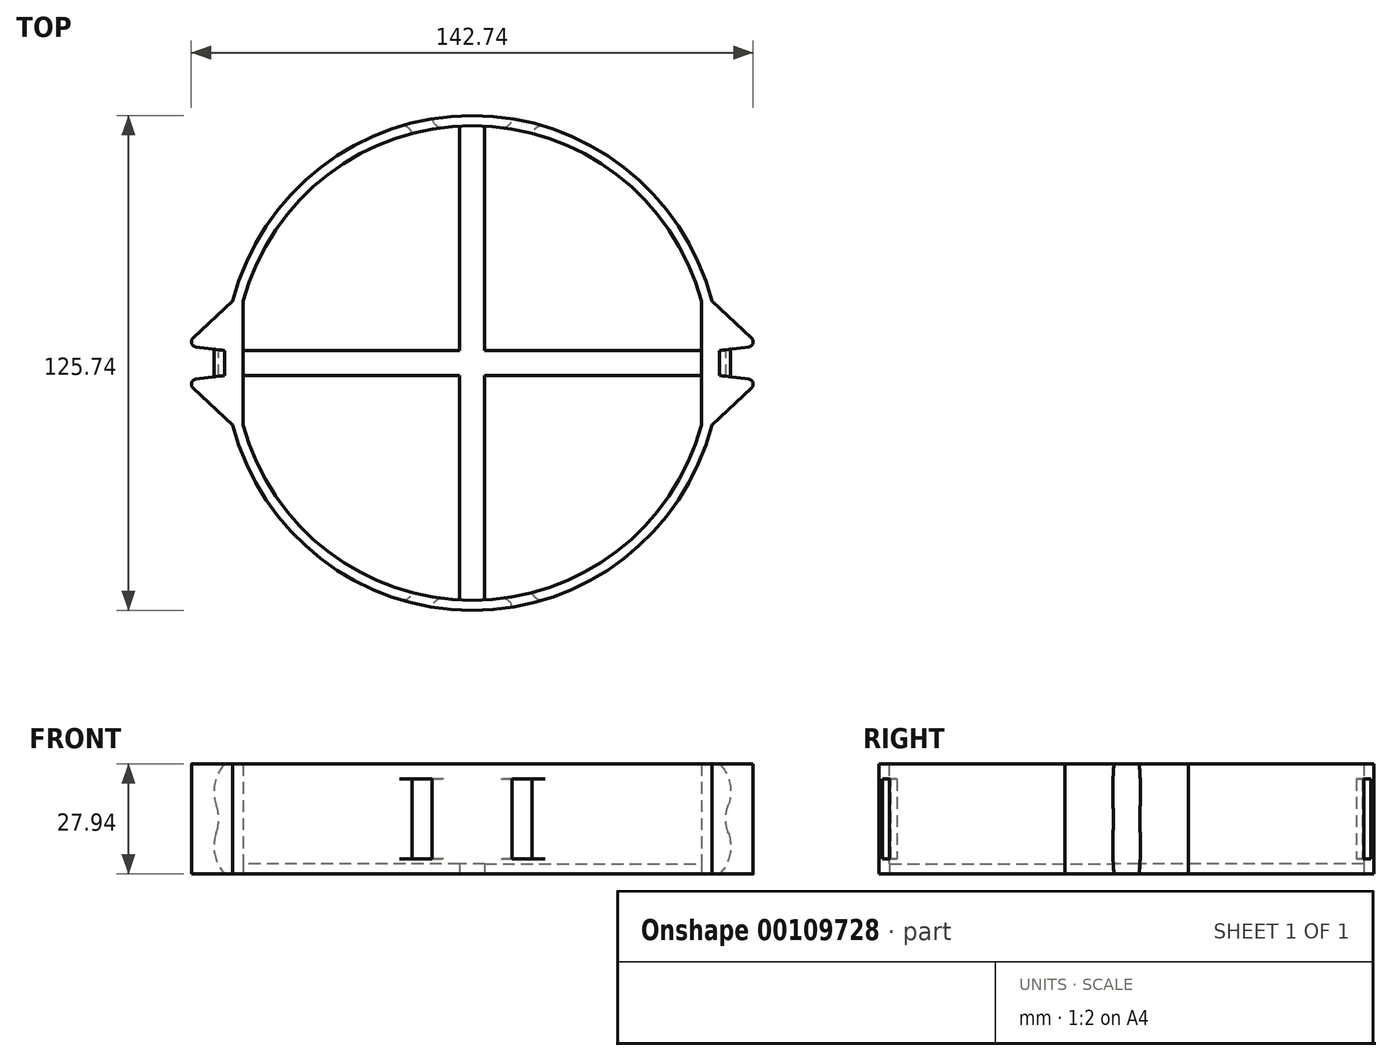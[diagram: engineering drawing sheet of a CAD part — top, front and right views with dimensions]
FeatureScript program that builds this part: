
annotation { "Feature Type Name" : "Feature", "Feature Type Description" : "" }
export const myFeature = defineFeature(function(context is Context, id is Id, definition is map)
    precondition{}
    {
        {
            var Q0;
            Q0=qCreatedBy(makeId("Top.planeOp"),FACE);
            var sketch = newSketch(context, id + "F0", { "sketchPlane" : qUnion([Q0])});
            skCircle(sketch, "E0", {"center": v(0, 0) * mm, "radius": 60.33 * mm});
            skCircle(sketch, "E1", {"center": v(0, 0) * mm, "radius": 62.87 * mm});
            skLineSegment(sketch, "E2", {"start": v(109.73, 0) * mm, "end": v(0, 0) * mm, "construction": true});
            skLineSegment(sketch, "E3", {"start": v(62.87, -3.18) * mm, "end": v(62.87, 3.17) * mm});
            skLineSegment(sketch, "E4", {"start": v(62.87, 3.17) * mm, "end": v(70.25, 4.1) * mm});
            skLineSegment(sketch, "E5", {"start": v(62.87, -3.18) * mm, "end": v(70.25, -4.1) * mm});
            skLineSegment(sketch, "E6", {"start": v(70.96, 6.3) * mm, "end": v(60.87, 15.7) * mm});
            skLineSegment(sketch, "E7", {"start": v(70.96, -6.3) * mm, "end": v(60.87, -15.7) * mm});
            skPoint(sketch, "E8.visualSharp", {"position": v(72.95, 4.44) * mm});
            skArc(sketch, "E8.filletArc", {"start": v(70.25, 4.1) * mm, "mid": v(71.3, 4.98) * mm, "end": v(70.96, 6.3) * mm});
            skPoint(sketch, "E9.visualSharp", {"position": v(72.95, -4.45) * mm});
            skArc(sketch, "E9.filletArc", {"start": v(70.96, -6.3) * mm, "mid": v(71.3, -4.98) * mm, "end": v(70.25, -4.1) * mm});
            skLineSegment(sketch, "E10", {"start": v(0, -72.25) * mm, "end": v(0, 0) * mm, "construction": true});
            skLineSegment(sketch, "E11.MirrorCS", {"start": v(-70.96, 6.3) * mm, "end": v(-60.87, 15.7) * mm});
            skArc(sketch, "E12.MirrorCS", {"start": v(-70.25, 4.1) * mm, "mid": v(-71.3, 4.98) * mm, "end": v(-70.96, 6.3) * mm});
            skLineSegment(sketch, "E13.MirrorCS", {"start": v(-62.87, -3.18) * mm, "end": v(-70.25, -4.1) * mm});
            skArc(sketch, "E14.MirrorCS", {"start": v(-70.96, -6.3) * mm, "mid": v(-71.3, -4.98) * mm, "end": v(-70.25, -4.1) * mm});
            skLineSegment(sketch, "E15.MirrorCS", {"start": v(-70.96, -6.3) * mm, "end": v(-60.87, -15.7) * mm});
            skLineSegment(sketch, "E16.MirrorCS", {"start": v(-62.87, 3.17) * mm, "end": v(-70.25, 4.1) * mm});
            skLineSegment(sketch, "E17", {"start": v(-62.87, -3.18) * mm, "end": v(-62.87, 3.17) * mm});
            skLineSegment(sketch, "E18", {"start": v(-60.87, 15.7) * mm, "end": v(-58.24, 15.7) * mm});
            skLineSegment(sketch, "E19", {"start": v(-60.87, -15.7) * mm, "end": v(-58.24, -15.7) * mm});
            skLineSegment(sketch, "E20", {"start": v(-58.24, -15.7) * mm, "end": v(-58.24, 15.7) * mm});
            skLineSegment(sketch, "E21", {"start": v(60.87, 15.7) * mm, "end": v(58.24, 15.7) * mm});
            skLineSegment(sketch, "E22", {"start": v(60.87, -15.7) * mm, "end": v(58.24, -15.7) * mm});
            skLineSegment(sketch, "E23", {"start": v(58.24, -15.7) * mm, "end": v(58.24, 15.7) * mm});
            skSolve(sketch);
        }
        {
            var Q0;
            {var subQ0=sQuery(id+"F0.wireOp",EDGE,"E15.MirrorCS");Q0=makeQuery(id+"F0.imprint","IMPRINT",FACE,{"disambiguationData":[TD([[makeQuery(id+"F0.imprint","IMPRINT",EDGE,{"derivedFrom":subQ0}),1.0]])]});}
            var Q1;
            Q1=makeQuery(id+"F0.imprint","IMPRINT",FACE,{"disambiguationData":[TD([[makeQuery(id+"F0.imprint","IMPRINT",EDGE,{"derivedFrom":sQuery(id+"F0.wireOp",EDGE,"E0")}),-1.0]])]});
            var Q2;
            {var subQ1=sQuery(id+"F0.wireOp",EDGE,"E4");Q2=makeQuery(id+"F0.imprint","IMPRINT",FACE,{"disambiguationData":[TD([[makeQuery(id+"F0.imprint","IMPRINT",EDGE,{"derivedFrom":subQ1}),1.0]])]});}
            var Q3;
            {var subQ1=sQuery(id+"F0.wireOp",EDGE,"E5");Q3=makeQuery(id+"F0.imprint","IMPRINT",FACE,{"disambiguationData":[TD([[makeQuery(id+"F0.imprint","IMPRINT",EDGE,{"derivedFrom":subQ1}),-1.0]])]});}
            var Q4;
            {var subQ0=sQuery(id+"F0.wireOp",EDGE,"E11.MirrorCS");Q4=makeQuery(id+"F0.imprint","IMPRINT",FACE,{"disambiguationData":[TD([[makeQuery(id+"F0.imprint","IMPRINT",EDGE,{"derivedFrom":subQ0}),-1.0]])]});}
            var Q5;
            {var subQ0=sQuery(id+"F0.wireOp",EDGE,"E23");Q5=makeQuery(id+"F0.imprint","IMPRINT",FACE,{"disambiguationData":[TD([[makeQuery(id+"F0.imprint","IMPRINT",EDGE,{"derivedFrom":subQ0}),-1.0]])]});}
            var Q6;
            {var subQ0=sQuery(id+"F0.wireOp",EDGE,"E21");Q6=makeQuery(id+"F0.imprint","IMPRINT",FACE,{"disambiguationData":[TD([[makeQuery(id+"F0.imprint","IMPRINT",EDGE,{"derivedFrom":subQ0}),1.0]])]});}
            var Q7;
            {var subQ0=sQuery(id+"F0.wireOp",EDGE,"E18");Q7=makeQuery(id+"F0.imprint","IMPRINT",FACE,{"disambiguationData":[TD([[makeQuery(id+"F0.imprint","IMPRINT",EDGE,{"derivedFrom":subQ0}),-1.0]])]});}
            var Q8;
            {var subQ0=sQuery(id+"F0.wireOp",EDGE,"E20");Q8=makeQuery(id+"F0.imprint","IMPRINT",FACE,{"disambiguationData":[TD([[makeQuery(id+"F0.imprint","IMPRINT",EDGE,{"derivedFrom":subQ0}),1.0]])]});}
            extrude(context, id + "F1", {"entities" : qUnion([Q0, Q1, Q2, Q3, Q4, Q5, Q6, Q7, Q8]), "depth" : 27.94 * mm});
        }
        {
            var Q0;
            Q0=makeQuery(id+"F1.opExtrude","CAP_FACE",FACE,{"disambiguationData":[OSD([sQuery(id+"F0.wireOp",EDGE,"E0"),sQuery(id+"F0.wireOp",EDGE,"E1"),sQuery(id+"F0.wireOp",EDGE,"E3"),sQuery(id+"F0.wireOp",EDGE,"E4"),sQuery(id+"F0.wireOp",EDGE,"E5"),sQuery(id+"F0.wireOp",EDGE,"E6"),sQuery(id+"F0.wireOp",EDGE,"E7"),sQuery(id+"F0.wireOp",EDGE,"E8.filletArc"),sQuery(id+"F0.wireOp",EDGE,"E9.filletArc"),sQuery(id+"F0.wireOp",EDGE,"E11.MirrorCS"),sQuery(id+"F0.wireOp",EDGE,"E15.MirrorCS"),sQuery(id+"F0.wireOp",EDGE,"E12.MirrorCS"),sQuery(id+"F0.wireOp",EDGE,"E16.MirrorCS"),sQuery(id+"F0.wireOp",EDGE,"E14.MirrorCS"),sQuery(id+"F0.wireOp",EDGE,"E13.MirrorCS"),sQuery(id+"F0.wireOp",EDGE,"E17"),sQuery(id+"F0.wireOp",EDGE,"E20"),sQuery(id+"F0.wireOp",EDGE,"E23")])],"isStart":true});
            var sketch = newSketch(context, id + "F2", { "sketchPlane" : qUnion([Q0])});
            skLineSegment(sketch, "E24.0", {"start": v(62.87, 3.18) * mm, "end": v(62.87, -3.17) * mm});
            skLineSegment(sketch, "E25.0", {"start": v(-62.87, 3.18) * mm, "end": v(-62.87, -3.17) * mm});
            skLineSegment(sketch, "E26", {"start": v(-62.87, 3.18) * mm, "end": v(62.87, 3.18) * mm});
            skLineSegment(sketch, "E27", {"start": v(62.87, -3.17) * mm, "end": v(-62.87, -3.18) * mm});
            skLineSegment(sketch, "E28", {"start": v(0, 0) * mm, "end": v(0, 111.99) * mm, "construction": true});
            skLineSegment(sketch, "E29", {"start": v(3.18, 3.18) * mm, "end": v(3.18, 60.24) * mm});
            skLineSegment(sketch, "E30", {"start": v(-3.18, 60.24) * mm, "end": v(-3.17, 3.18) * mm});
            skLineSegment(sketch, "E31", {"start": v(-3.17, 3.18) * mm, "end": v(-3.17, -60.24) * mm});
            skLineSegment(sketch, "E32", {"start": v(3.18, -60.24) * mm, "end": v(3.18, 3.18) * mm});
            skSolve(sketch);
        }
        {
            var Q0;
            Q0 = qSketchRegion(id + "F2", true);
            var Q1;
            {var subQ0=sQuery(id+"F2.wireOp",EDGE,"E29");Q1=makeQuery(id+"F2.imprint","IMPRINT",FACE,{"disambiguationData":[TD([[makeQuery(id+"F2.imprint","IMPRINT",EDGE,{"derivedFrom":subQ0}),1.0]])]});}
            var Q2;
            {var subQ0=sQuery(id+"F2.wireOp",EDGE,"E32");var subQ1=sQuery(id+"F2.wireOp",EDGE,"E27");var subQ2=makeQuery(id+"F2.imprint","INTERSECT",VERTEX,{"derivedFrom":[subQ1,subQ0]});Q2=makeQuery(id+"F2.imprint","IMPRINT",FACE,{"disambiguationData":[TD([[makeQuery(id+"F2.imprint","IMPRINT",EDGE,{"disambiguationData":[TD([[subQ2,-1.0]])],"derivedFrom":subQ1}),1.0]])]});}
            extrude(context, id + "F3", {"entities" : qUnion([Q0, Q1, Q2]), "operationType" : NewBodyOperationType.ADD, "oppositeDirection" : true, "depth" : 2.54 * mm});
        }
        {
            var Q0;
            Q0=qCreatedBy(makeId("Front.planeOp"),FACE);
            var sketch = newSketch(context, id + "F4", { "sketchPlane" : qUnion([Q0])});
            skLineSegment(sketch, "E33.bottom", {"start": v(-10.16, 24.13) * mm, "end": v(-15.24, 24.13) * mm});
            skLineSegment(sketch, "E33.top", {"start": v(-10.16, 3.8) * mm, "end": v(-15.24, 3.8) * mm});
            skLineSegment(sketch, "E33.left", {"start": v(-10.16, 24.13) * mm, "end": v(-10.16, 3.8) * mm});
            skLineSegment(sketch, "E33.right", {"start": v(-15.24, 24.13) * mm, "end": v(-15.24, 3.8) * mm});
            skLineSegment(sketch, "E34.bottom", {"start": v(10.16, 24.13) * mm, "end": v(15.24, 24.13) * mm});
            skLineSegment(sketch, "E34.top", {"start": v(10.16, 3.81) * mm, "end": v(15.24, 3.81) * mm});
            skLineSegment(sketch, "E34.left", {"start": v(10.16, 24.13) * mm, "end": v(10.16, 3.81) * mm});
            skLineSegment(sketch, "E34.right", {"start": v(15.24, 24.13) * mm, "end": v(15.24, 3.81) * mm});
            skSolve(sketch);
        }
        {
            var Q0;
            Q0 = qSketchRegion(id + "F4", true);
            extrude(context, id + "F5", {"entities" : qUnion([Q0]), "operationType" : NewBodyOperationType.REMOVE, "endBound" : BoundingType.THROUGH_ALL, "oppositeDirection" : true, "depth" : 25.4 * mm, "hasSecondDirection" : true, "secondDirectionBound" : SecondDirectionBoundingType.THROUGH_ALL, "secondDirectionOppositeDirection" : false, "secondDirectionDepth" : 25.4 * mm});
        }
        {
            var Q0;
            {var subQ0=sQuery(id+"F0.wireOp",EDGE,"E1");Q0=makeQuery(id+"F5.boolean.opBoolean","INTERSECT",EDGE,{"derivedFrom":[makeQuery(id+"F1.opExtrude","SWEPT_FACE",FACE,{"disambiguationData":[OSD([subQ0]),TDD([makeQuery(id+"F0.imprint","IMPRINT",EDGE,{"disambiguationData":[TD([[makeQuery(id+"F0.imprint","INTERSECT",VERTEX,{"derivedFrom":[subQ0,sQuery(id+"F0.wireOp",EDGE,"E6"),sQuery(id+"F0.wireOp",EDGE,"E21")]}),-1.0]])],"derivedFrom":subQ0})])]}),makeQuery(id+"F5.opExtrude","SWEPT_FACE",FACE,{"disambiguationData":[OSD([sQuery(id+"F4.wireOp",EDGE,"E34.right")])]})]});}
            var Q1;
            {var subQ0=sQuery(id+"F0.wireOp",EDGE,"E1");Q1=makeQuery(id+"F5.boolean.opBoolean","INTERSECT",EDGE,{"derivedFrom":[makeQuery(id+"F1.opExtrude","SWEPT_FACE",FACE,{"disambiguationData":[OSD([subQ0]),TDD([makeQuery(id+"F0.imprint","IMPRINT",EDGE,{"disambiguationData":[TD([[makeQuery(id+"F0.imprint","INTERSECT",VERTEX,{"derivedFrom":[subQ0,sQuery(id+"F0.wireOp",EDGE,"E6"),sQuery(id+"F0.wireOp",EDGE,"E21")]}),-1.0]])],"derivedFrom":subQ0})])]}),makeQuery(id+"F5.opExtrude","SWEPT_FACE",FACE,{"disambiguationData":[OSD([sQuery(id+"F4.wireOp",EDGE,"E33.right")])]})]});}
            var Q2;
            {var subQ0=sQuery(id+"F0.wireOp",EDGE,"E0");Q2=makeQuery(id+"F5.boolean.opBoolean","INTERSECT",EDGE,{"derivedFrom":[makeQuery(id+"F1.opExtrude","SWEPT_FACE",FACE,{"disambiguationData":[OSD([subQ0]),TDD([makeQuery(id+"F0.imprint","IMPRINT",EDGE,{"disambiguationData":[TD([[makeQuery(id+"F0.imprint","INTERSECT",VERTEX,{"derivedFrom":[subQ0,sQuery(id+"F0.wireOp",EDGE,"E18"),sQuery(id+"F0.wireOp",EDGE,"E20")]}),1.0]])],"derivedFrom":subQ0})])]}),makeQuery(id+"F5.opExtrude","SWEPT_FACE",FACE,{"disambiguationData":[OSD([sQuery(id+"F4.wireOp",EDGE,"E34.left")])]})]});}
            var Q3;
            {var subQ0=sQuery(id+"F0.wireOp",EDGE,"E0");Q3=makeQuery(id+"F5.boolean.opBoolean","INTERSECT",EDGE,{"derivedFrom":[makeQuery(id+"F1.opExtrude","SWEPT_FACE",FACE,{"disambiguationData":[OSD([subQ0]),TDD([makeQuery(id+"F0.imprint","IMPRINT",EDGE,{"disambiguationData":[TD([[makeQuery(id+"F0.imprint","INTERSECT",VERTEX,{"derivedFrom":[subQ0,sQuery(id+"F0.wireOp",EDGE,"E18"),sQuery(id+"F0.wireOp",EDGE,"E20")]}),1.0]])],"derivedFrom":subQ0})])]}),makeQuery(id+"F5.opExtrude","SWEPT_FACE",FACE,{"disambiguationData":[OSD([sQuery(id+"F4.wireOp",EDGE,"E33.left")])]})]});}
            var Q4;
            {var subQ0=sQuery(id+"F0.wireOp",EDGE,"E1");Q4=makeQuery(id+"F5.boolean.opBoolean","INTERSECT",EDGE,{"derivedFrom":[makeQuery(id+"F1.opExtrude","SWEPT_FACE",FACE,{"disambiguationData":[OSD([subQ0]),TDD([makeQuery(id+"F0.imprint","IMPRINT",EDGE,{"disambiguationData":[TD([[makeQuery(id+"F0.imprint","INTERSECT",VERTEX,{"derivedFrom":[subQ0,sQuery(id+"F0.wireOp",EDGE,"E7"),sQuery(id+"F0.wireOp",EDGE,"E22")]}),1.0]])],"derivedFrom":subQ0})])]}),makeQuery(id+"F5.opExtrude","SWEPT_FACE",FACE,{"disambiguationData":[OSD([sQuery(id+"F4.wireOp",EDGE,"E33.right")])]})]});}
            var Q5;
            {var subQ0=sQuery(id+"F0.wireOp",EDGE,"E1");Q5=makeQuery(id+"F5.boolean.opBoolean","INTERSECT",EDGE,{"derivedFrom":[makeQuery(id+"F1.opExtrude","SWEPT_FACE",FACE,{"disambiguationData":[OSD([subQ0]),TDD([makeQuery(id+"F0.imprint","IMPRINT",EDGE,{"disambiguationData":[TD([[makeQuery(id+"F0.imprint","INTERSECT",VERTEX,{"derivedFrom":[subQ0,sQuery(id+"F0.wireOp",EDGE,"E7"),sQuery(id+"F0.wireOp",EDGE,"E22")]}),1.0]])],"derivedFrom":subQ0})])]}),makeQuery(id+"F5.opExtrude","SWEPT_FACE",FACE,{"disambiguationData":[OSD([sQuery(id+"F4.wireOp",EDGE,"E34.right")])]})]});}
            var Q6;
            {var subQ0=sQuery(id+"F0.wireOp",EDGE,"E0");Q6=makeQuery(id+"F5.boolean.opBoolean","INTERSECT",EDGE,{"derivedFrom":[makeQuery(id+"F1.opExtrude","SWEPT_FACE",FACE,{"disambiguationData":[OSD([subQ0]),TDD([makeQuery(id+"F0.imprint","IMPRINT",EDGE,{"disambiguationData":[TD([[makeQuery(id+"F0.imprint","INTERSECT",VERTEX,{"derivedFrom":[subQ0,sQuery(id+"F0.wireOp",EDGE,"E19"),sQuery(id+"F0.wireOp",EDGE,"E20")]}),-1.0]])],"derivedFrom":subQ0})])]}),makeQuery(id+"F5.opExtrude","SWEPT_FACE",FACE,{"disambiguationData":[OSD([sQuery(id+"F4.wireOp",EDGE,"E34.left")])]})]});}
            var Q7;
            {var subQ0=sQuery(id+"F0.wireOp",EDGE,"E0");Q7=makeQuery(id+"F5.boolean.opBoolean","INTERSECT",EDGE,{"derivedFrom":[makeQuery(id+"F1.opExtrude","SWEPT_FACE",FACE,{"disambiguationData":[OSD([subQ0]),TDD([makeQuery(id+"F0.imprint","IMPRINT",EDGE,{"disambiguationData":[TD([[makeQuery(id+"F0.imprint","INTERSECT",VERTEX,{"derivedFrom":[subQ0,sQuery(id+"F0.wireOp",EDGE,"E19"),sQuery(id+"F0.wireOp",EDGE,"E20")]}),-1.0]])],"derivedFrom":subQ0})])]}),makeQuery(id+"F5.opExtrude","SWEPT_FACE",FACE,{"disambiguationData":[OSD([sQuery(id+"F4.wireOp",EDGE,"E33.left")])]})]});}
            fillet(context, id + "F6", {"entities" : qUnion([Q0, Q1, Q2, Q3, Q4, Q5, Q6, Q7]), "radius" : 2.54 * mm, "tangentPropagation" : true, "allowEdgeOverflow" : false});
        }
        {
            var Q0;
            Q0=qCreatedBy(makeId("Front.planeOp"),FACE);
            var sketch = newSketch(context, id + "F7", { "sketchPlane" : qUnion([Q0])});
            skLineSegment(sketch, "E35.0.3", {"start": v(62.87, 27.94) * mm, "end": v(62.87, 0) * mm});
            skLineSegment(sketch, "E36.0.1", {"start": v(-62.87, 0) * mm, "end": v(-62.87, 27.94) * mm});
            skArc(sketch, "E37", {"start": v(65.03, 17.46) * mm, "mid": v(65.44, 23) * mm, "end": v(62.87, 27.94) * mm});
            skArc(sketch, "E38", {"start": v(62.87, 0) * mm, "mid": v(65.44, 4.93) * mm, "end": v(65.03, 10.48) * mm});
            skPoint(sketch, "E39.visualSharp", {"position": v(62.87, 13.97) * mm});
            skArc(sketch, "E39.filletArc", {"start": v(65.03, 17.46) * mm, "mid": v(64.4, 13.97) * mm, "end": v(65.03, 10.48) * mm});
            skLineSegment(sketch, "E40", {"start": v(0, 0) * mm, "end": v(0, 50.99) * mm, "construction": true});
            skArc(sketch, "E41.MirrorCS", {"start": v(-62.87, 0) * mm, "mid": v(-65.44, 4.93) * mm, "end": v(-65.03, 10.48) * mm});
            skArc(sketch, "E42.MirrorCS", {"start": v(-65.03, 17.46) * mm, "mid": v(-64.4, 13.97) * mm, "end": v(-65.03, 10.48) * mm});
            skArc(sketch, "E43.MirrorCS", {"start": v(-65.03, 17.46) * mm, "mid": v(-65.44, 23) * mm, "end": v(-62.87, 27.94) * mm});
            skSolve(sketch);
        }
        {
            var Q0;
            Q0 = qSketchRegion(id + "F7", true);
            var Q1;
            Q1=makeQuery(id+"F1.opExtrude","SWEPT_FACE",FACE,{"disambiguationData":[OSD([sQuery(id+"F0.wireOp",EDGE,"E5")])]});
            extrude(context, id + "F8", {"entities" : qUnion([Q0]), "operationType" : NewBodyOperationType.ADD, "endBound" : BoundingType.UP_TO_NEXT, "depth" : 25.4 * mm, "hasSecondDirection" : true, "secondDirectionBound" : SecondDirectionBoundingType.UP_TO_NEXT, "secondDirectionOppositeDirection" : true, "secondDirectionBoundEntityFace" : qUnion([Q1]), "secondDirectionDepth" : 25.4 * mm});
        }
    });
